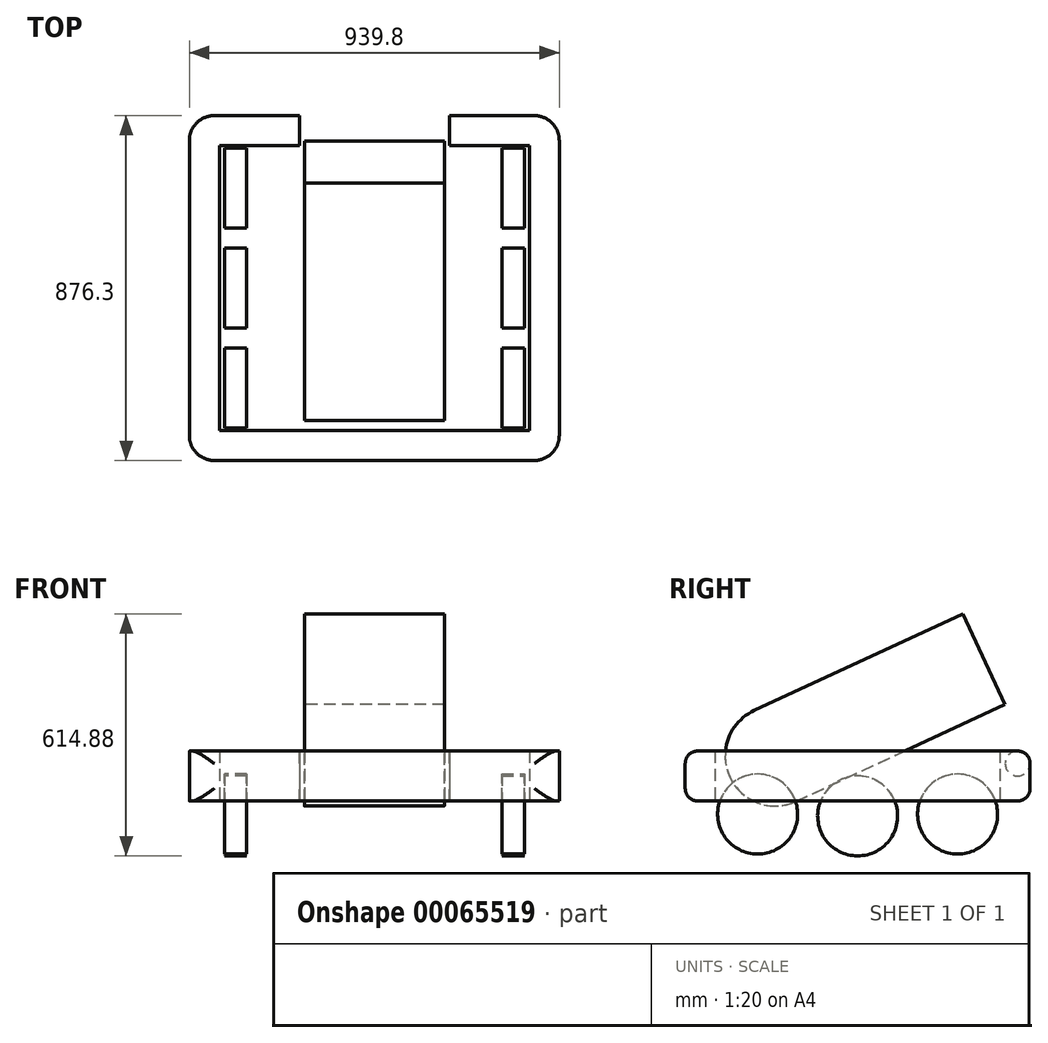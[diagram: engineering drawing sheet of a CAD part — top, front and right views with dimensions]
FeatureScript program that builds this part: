
annotation { "Feature Type Name" : "Feature", "Feature Type Description" : "" }
export const myFeature = defineFeature(function(context is Context, id is Id, definition is map)
    precondition{}
    {
        {
            var Q0;
            Q0=qCreatedBy(makeId("Top.planeOp"),FACE);
            var sketch = newSketch(context, id + "F0", { "sketchPlane" : qUnion([Q0])});
            skLineSegment(sketch, "E0.bottom", {"start": v(-393.7, 361.95) * mm, "end": v(393.7, 361.95) * mm});
            skLineSegment(sketch, "E0.top", {"start": v(-393.7, -361.95) * mm, "end": v(393.7, -361.95) * mm});
            skLineSegment(sketch, "E0.left", {"start": v(-393.7, 361.95) * mm, "end": v(-393.7, -361.95) * mm});
            skLineSegment(sketch, "E0.right", {"start": v(393.7, 361.95) * mm, "end": v(393.7, -361.95) * mm});
            skLineSegment(sketch, "E1", {"start": v(0, 361.95) * mm, "end": v(0, -361.95) * mm, "construction": true});
            skCircle(sketch, "E2", {"center": v(-1228.9, -799.4) * mm, "radius": 127 * mm});
            skCircle(sketch, "E3", {"center": v(0, -155.3) * mm, "radius": 127 * mm});
            skLineSegment(sketch, "E4.bottom", {"start": v(-381, 349.25) * mm, "end": v(-342.9, 349.25) * mm});
            skLineSegment(sketch, "E4.top", {"start": v(-381, 44.45) * mm, "end": v(-342.9, 44.45) * mm});
            skLineSegment(sketch, "E4.left", {"start": v(-381, 349.25) * mm, "end": v(-381, 44.45) * mm});
            skLineSegment(sketch, "E4.right", {"start": v(-342.9, 349.25) * mm, "end": v(-342.9, 44.45) * mm});
            skLineSegment(sketch, "E5.bottom", {"start": v(-381, -44.45) * mm, "end": v(-342.9, -44.45) * mm});
            skLineSegment(sketch, "E5.top", {"start": v(-381, -349.25) * mm, "end": v(-342.9, -349.25) * mm});
            skLineSegment(sketch, "E5.left", {"start": v(-381, -44.45) * mm, "end": v(-381, -349.25) * mm});
            skLineSegment(sketch, "E5.right", {"start": v(-342.9, -44.45) * mm, "end": v(-342.9, -349.25) * mm});
            skLineSegment(sketch, "E6.bottom", {"start": v(342.9, 349.25) * mm, "end": v(381, 349.25) * mm});
            skLineSegment(sketch, "E6.top", {"start": v(342.9, 44.45) * mm, "end": v(381, 44.45) * mm});
            skLineSegment(sketch, "E6.left", {"start": v(342.9, 349.25) * mm, "end": v(342.9, 44.45) * mm});
            skLineSegment(sketch, "E6.right", {"start": v(381, 349.25) * mm, "end": v(381, 44.45) * mm});
            skLineSegment(sketch, "E7.bottom", {"start": v(342.9, -44.45) * mm, "end": v(381, -44.45) * mm});
            skLineSegment(sketch, "E7.top", {"start": v(342.9, -349.25) * mm, "end": v(381, -349.25) * mm});
            skLineSegment(sketch, "E7.left", {"start": v(342.9, -44.45) * mm, "end": v(342.9, -349.25) * mm});
            skLineSegment(sketch, "E7.right", {"start": v(381, -44.45) * mm, "end": v(381, -349.25) * mm});
            skLineSegment(sketch, "E8", {"start": v(393.7, 0) * mm, "end": v(-393.7, 0) * mm, "construction": true});
            skLineSegment(sketch, "E9.bottom", {"start": v(-406.4, 438.15) * mm, "end": v(-190.5, 438.15) * mm});
            skLineSegment(sketch, "E9.top", {"start": v(-406.4, -438.15) * mm, "end": v(406.4, -438.15) * mm});
            skLineSegment(sketch, "E9.left", {"start": v(-469.9, 374.65) * mm, "end": v(-469.9, -374.65) * mm});
            skLineSegment(sketch, "E9.right", {"start": v(469.9, 374.65) * mm, "end": v(469.9, -374.65) * mm});
            skPoint(sketch, "E10.visualSharp", {"position": v(-469.9, 438.15) * mm});
            skArc(sketch, "E10.filletArc", {"start": v(-406.4, 438.15) * mm, "mid": v(-451.3, 419.55) * mm, "end": v(-469.9, 374.65) * mm});
            skPoint(sketch, "E11.visualSharp", {"position": v(-469.9, -438.15) * mm});
            skArc(sketch, "E11.filletArc", {"start": v(-469.9, -374.65) * mm, "mid": v(-451.3, -419.55) * mm, "end": v(-406.4, -438.15) * mm});
            skPoint(sketch, "E12.visualSharp", {"position": v(469.9, -438.15) * mm});
            skArc(sketch, "E12.filletArc", {"start": v(406.4, -438.15) * mm, "mid": v(451.3, -419.55) * mm, "end": v(469.9, -374.65) * mm});
            skPoint(sketch, "E13.visualSharp", {"position": v(469.9, 438.15) * mm});
            skArc(sketch, "E13.filletArc", {"start": v(469.9, 374.65) * mm, "mid": v(451.3, 419.55) * mm, "end": v(406.4, 438.15) * mm});
            skLineSegment(sketch, "E14", {"start": v(-1228.9, -799.4) * mm, "end": v(-505, -799.4) * mm});
            skLineSegment(sketch, "E15", {"start": v(-505, -799.4) * mm, "end": v(282.4, -799.4) * mm});
            skLineSegment(sketch, "E16", {"start": v(190.5, 438.15) * mm, "end": v(190.5, 361.95) * mm});
            skLineSegment(sketch, "E17", {"start": v(-190.5, 438.15) * mm, "end": v(-190.5, 361.95) * mm});
            skLineSegment(sketch, "E18.trimOffspring", {"start": v(190.5, 438.15) * mm, "end": v(406.4, 438.15) * mm});
            skLineSegment(sketch, "E19", {"start": v(-342.9, 196.85) * mm, "end": v(-381, 196.85) * mm, "construction": true});
            skLineSegment(sketch, "E20", {"start": v(-342.9, -196.85) * mm, "end": v(-381, -196.85) * mm, "construction": true});
            skSolve(sketch);
        }
        {
            var Q0;
            Q0=qCreatedBy(makeId("Right.planeOp"),FACE);
            var sketch = newSketch(context, id + "F1", { "sketchPlane" : qUnion([Q0])});
            skCircle(sketch, "E21", {"center": v(196.85, 0) * mm, "radius": 152.4 * mm, "construction": true});
            skCircle(sketch, "E22", {"center": v(-196.85, 0) * mm, "radius": 152.4 * mm, "construction": true});
            skLineSegment(sketch, "E23.0", {"start": v(-44.45, 0) * mm, "end": v(-349.25, 0) * mm, "construction": true});
            skLineSegment(sketch, "E23.1", {"start": v(349.25, 0) * mm, "end": v(44.45, 0) * mm, "construction": true});
            skLineSegment(sketch, "E24.bottom", {"start": v(406.4, 114.3) * mm, "end": v(-406.4, 114.3) * mm});
            skLineSegment(sketch, "E24.top", {"start": v(406.4, -12.7) * mm, "end": v(-406.4, -12.7) * mm});
            skLineSegment(sketch, "E24.left", {"start": v(438.15, 82.55) * mm, "end": v(438.15, 19.05) * mm});
            skLineSegment(sketch, "E24.right", {"start": v(-438.15, 82.55) * mm, "end": v(-438.15, 19.05) * mm});
            skLineSegment(sketch, "E25", {"start": v(-789.47, -152.4) * mm, "end": v(789.47, -152.4) * mm, "construction": true});
            skPoint(sketch, "E26.visualSharp", {"position": v(438.15, 114.3) * mm});
            skArc(sketch, "E26.filletArc", {"start": v(438.15, 82.55) * mm, "mid": v(428.85, 105) * mm, "end": v(406.4, 114.3) * mm});
            skPoint(sketch, "E27.visualSharp", {"position": v(438.15, -12.7) * mm});
            skArc(sketch, "E27.filletArc", {"start": v(406.4, -12.7) * mm, "mid": v(428.85, -3.4) * mm, "end": v(438.15, 19.05) * mm});
            skPoint(sketch, "E28.visualSharp", {"position": v(-438.15, -12.7) * mm});
            skArc(sketch, "E28.filletArc", {"start": v(-438.15, 19.05) * mm, "mid": v(-428.85, -3.4) * mm, "end": v(-406.4, -12.7) * mm});
            skPoint(sketch, "E29.visualSharp", {"position": v(-438.15, 114.3) * mm});
            skArc(sketch, "E29.filletArc", {"start": v(-406.4, 114.3) * mm, "mid": v(-428.85, 105) * mm, "end": v(-438.15, 82.55) * mm});
            skPoint(sketch, "E30", {"position": v(0, -152.4) * mm});
            skLineSegment(sketch, "E31.bottom", {"start": v(1733.48, -38.1) * mm, "end": v(1619.18, -38.1) * mm});
            skLineSegment(sketch, "E31.top", {"start": v(1733.48, -152.4) * mm, "end": v(1619.18, -152.4) * mm});
            skLineSegment(sketch, "E31.left", {"start": v(1733.48, -38.1) * mm, "end": v(1733.48, -152.4) * mm});
            skLineSegment(sketch, "E31.right", {"start": v(1619.18, -38.1) * mm, "end": v(1619.18, -152.4) * mm});
            skLineSegment(sketch, "E32", {"start": v(361.95, 241.3) * mm, "end": v(-361.95, 241.3) * mm});
            skCircle(sketch, "E33", {"center": v(0, 266.7) * mm, "radius": 12.7 * mm});
            skLineSegment(sketch, "E34.bottom", {"start": v(1878.31, -88.9) * mm, "end": v(1840.21, -88.9) * mm});
            skLineSegment(sketch, "E34.top", {"start": v(1878.31, -152.4) * mm, "end": v(1840.21, -152.4) * mm});
            skLineSegment(sketch, "E34.left", {"start": v(1878.31, -88.9) * mm, "end": v(1878.31, -152.4) * mm});
            skLineSegment(sketch, "E34.right", {"start": v(1840.21, -88.9) * mm, "end": v(1840.21, -152.4) * mm});
            skLineSegment(sketch, "E35", {"start": v(535.67, -152.4) * mm, "end": v(535.67, -73.87) * mm});
            skLineSegment(sketch, "E36", {"start": v(535.67, -73.87) * mm, "end": v(1094.47, -152.4) * mm});
            skPoint(sketch, "E36.endSnap0", {"position": v(1859.26, -152.4) * mm});
            skPoint(sketch, "E37", {"position": v(1676.33, -152.4) * mm});
            skLineSegment(sketch, "E38", {"start": v(0, 266.7) * mm, "end": v(-373.39, 342.49) * mm});
            skCircle(sketch, "E39", {"center": v(-373.39, 342.49) * mm, "radius": 12.7 * mm});
            skLineSegment(sketch, "E40.bottom", {"start": v(1374, -152.4) * mm, "end": v(1450.2, -152.4) * mm});
            skLineSegment(sketch, "E40.top", {"start": v(1374, -76.2) * mm, "end": v(1450.2, -76.2) * mm});
            skLineSegment(sketch, "E40.left", {"start": v(1374, -152.4) * mm, "end": v(1374, -76.2) * mm});
            skLineSegment(sketch, "E40.right", {"start": v(1450.2, -152.4) * mm, "end": v(1450.2, -76.2) * mm});
            skLineSegment(sketch, "E41", {"start": v(-61.4, -69.85) * mm, "end": v(61.4, -69.85) * mm});
            skCircle(sketch, "E42", {"center": v(-663.32, -25.4) * mm, "radius": 127 * mm});
            skCircle(sketch, "E43", {"center": v(3436.9, 34.7) * mm, "radius": 39.75 * mm});
            skCircle(sketch, "E44", {"center": v(3218.47, -112.65) * mm, "radius": 39.75 * mm});
            skCircle(sketch, "E45", {"center": v(2761.27, -112.65) * mm, "radius": 39.75 * mm});
            skLineSegment(sketch, "E46", {"start": v(2761.27, -112.65) * mm, "end": v(3218.47, -112.65) * mm, "construction": true});
            skLineSegment(sketch, "E47", {"start": v(3436.9, 34.7) * mm, "end": v(3218.47, -112.65) * mm, "construction": true});
            skLineSegment(sketch, "E48", {"start": v(3459.14, 1.74) * mm, "end": v(3240.7, -145.6) * mm});
            skLineSegment(sketch, "E49", {"start": v(3428.44, 73.53) * mm, "end": v(2752.8, -73.81) * mm});
            skLineSegment(sketch, "E50.bottom", {"start": v(2348.21, -88.9) * mm, "end": v(2310.11, -88.9) * mm});
            skLineSegment(sketch, "E50.top", {"start": v(2348.21, -152.4) * mm, "end": v(2310.11, -152.4) * mm});
            skLineSegment(sketch, "E50.left", {"start": v(2348.21, -88.9) * mm, "end": v(2348.21, -152.4) * mm});
            skLineSegment(sketch, "E50.right", {"start": v(2310.11, -88.9) * mm, "end": v(2310.11, -152.4) * mm});
            skCircle(sketch, "E51", {"center": v(2989.87, -112.65) * mm, "radius": 39.75 * mm});
            skLineSegment(sketch, "E52", {"start": v(2761.27, -152.4) * mm, "end": v(3218.47, -152.4) * mm});
            skSolve(sketch);
        }
        {
            var Q0;
            Q0=qCreatedBy(makeId("Top.planeOp"),FACE);
            var sketch = newSketch(context, id + "F2", { "sketchPlane" : qUnion([Q0])});
            skLineSegment(sketch, "E53.bottom", {"start": v(-4052.58, 2835.77) * mm, "end": v(4050.02, 2835.77) * mm});
            skLineSegment(sketch, "E53.top", {"start": v(-4050.02, -13648.83) * mm, "end": v(4050.02, -13648.83) * mm});
            skLineSegment(sketch, "E53.right", {"start": v(4050.02, 2835.77) * mm, "end": v(4050.02, -13648.83) * mm});
            skLineSegment(sketch, "E54", {"start": v(-4052.58, 2835.77) * mm, "end": v(-4052.58, -2659.1) * mm});
            skLineSegment(sketch, "E55", {"start": v(-4052.58, -2659.1) * mm, "end": v(-4052.58, -8153.97) * mm});
            skLineSegment(sketch, "E56", {"start": v(-4052.58, -8153.97) * mm, "end": v(-4050.02, -13648.83) * mm});
            skLineSegment(sketch, "E57", {"start": v(-2376.18, -8153.97) * mm, "end": v(4050.02, -8153.97) * mm, "construction": true});
            skLineSegment(sketch, "E58", {"start": v(-4052.58, -2659.1) * mm, "end": v(2373.62, -2659.1) * mm, "construction": true});
            skLineSegment(sketch, "E59.bottom", {"start": v(2373.62, -2058.4) * mm, "end": v(-4052.58, -2058.4) * mm});
            skLineSegment(sketch, "E59.top", {"start": v(2373.62, -3259.81) * mm, "end": v(-4052.58, -3259.81) * mm});
            skLineSegment(sketch, "E59.right", {"start": v(-4052.58, -2058.4) * mm, "end": v(-4052.58, -3259.81) * mm});
            skLineSegment(sketch, "E60.bottom", {"start": v(4050.02, -8754.68) * mm, "end": v(-2376.18, -8754.68) * mm});
            skLineSegment(sketch, "E60.top", {"start": v(4050.02, -7553.26) * mm, "end": v(-2376.18, -7553.26) * mm});
            skLineSegment(sketch, "E60.left", {"start": v(4050.02, -8754.68) * mm, "end": v(4050.02, -7553.26) * mm});
            skLineSegment(sketch, "E61", {"start": v(0, 2835.77) * mm, "end": v(0, -13648.83) * mm, "construction": true});
            skLineSegment(sketch, "E62", {"start": v(-609.6, 2835.77) * mm, "end": v(-304.8, 2307.84) * mm, "construction": true});
            skLineSegment(sketch, "E63", {"start": v(-304.8, 2307.84) * mm, "end": v(304.8, 2307.84) * mm, "construction": true});
            skLineSegment(sketch, "E64", {"start": v(304.8, 2307.84) * mm, "end": v(609.6, 2835.77) * mm, "construction": true});
            skLineSegment(sketch, "E65", {"start": v(2373.62, 2835.77) * mm, "end": v(2373.62, -4466.73) * mm});
            skLineSegment(sketch, "E66", {"start": v(2373.62, -4466.73) * mm, "end": v(4050.02, -4466.73) * mm});
            skLineSegment(sketch, "E67", {"start": v(-4052.58, -6346.33) * mm, "end": v(-2376.18, -6346.33) * mm});
            skLineSegment(sketch, "E68", {"start": v(-2376.18, -6346.33) * mm, "end": v(-2376.18, -13648.83) * mm});
            skLineSegment(sketch, "E69", {"start": v(-762, 2835.77) * mm, "end": v(-381, 2175.85) * mm});
            skLineSegment(sketch, "E70", {"start": v(-381, 2175.85) * mm, "end": v(381, 2175.85) * mm});
            skLineSegment(sketch, "E71", {"start": v(381, 2175.85) * mm, "end": v(762, 2835.77) * mm});
            skLineSegment(sketch, "E72", {"start": v(-1533.48, 2835.77) * mm, "end": v(-1533.48, 2302.37) * mm});
            skLineSegment(sketch, "E73", {"start": v(-1533.48, 2302.37) * mm, "end": v(-1228.68, 1774.44) * mm});
            skLineSegment(sketch, "E74", {"start": v(-1228.68, 1774.44) * mm, "end": v(-304.8, 1241.04) * mm});
            skLineSegment(sketch, "E75", {"start": v(-304.8, 1241.04) * mm, "end": v(304.8, 1241.04) * mm});
            skLineSegment(sketch, "E76", {"start": v(304.8, 1241.04) * mm, "end": v(1228.68, 1774.44) * mm});
            skLineSegment(sketch, "E77", {"start": v(1228.68, 1774.44) * mm, "end": v(1533.48, 2302.37) * mm});
            skLineSegment(sketch, "E78", {"start": v(1533.48, 2302.37) * mm, "end": v(1533.48, 2835.77) * mm});
            skLineSegment(sketch, "E79", {"start": v(457.2, 2571.8) * mm, "end": v(1381.08, 2038.4) * mm, "construction": true});
            skLineSegment(sketch, "E80", {"start": v(0, 2307.84) * mm, "end": v(0, 1241.04) * mm, "construction": true});
            skArc(sketch, "E81", {"start": v(-2032, 2835.77) * mm, "mid": v(0, 803.77) * mm, "end": v(2032, 2835.77) * mm, "construction": true});
            skArc(sketch, "E82", {"start": v(-4052.58, -1011.62) * mm, "mid": v(-1.85, -2752.23) * mm, "end": v(4050.02, -1014.3) * mm, "construction": true});
            skArc(sketch, "E83", {"start": v(-762, 2835.77) * mm, "mid": v(0, 2073.77) * mm, "end": v(762, 2835.77) * mm, "construction": true});
            skSolve(sketch);
        }
        {
            var Q0;
            Q0=qCreatedBy(makeId("Right.planeOp"),FACE);
            var sketch = newSketch(context, id + "F3", { "sketchPlane" : qUnion([Q0])});
            skLineSegment(sketch, "E84.bottom", {"start": v(406.4, 114.3) * mm, "end": v(-406.4, 114.3) * mm, "construction": true});
            skLineSegment(sketch, "E84.top", {"start": v(406.4, -12.7) * mm, "end": v(-406.4, -12.7) * mm, "construction": true});
            skLineSegment(sketch, "E84.left", {"start": v(438.15, 82.55) * mm, "end": v(438.15, 19.05) * mm, "construction": true});
            skLineSegment(sketch, "E84.right", {"start": v(-438.15, 82.55) * mm, "end": v(-438.15, 19.05) * mm, "construction": true});
            skPoint(sketch, "E85.visualSharp", {"position": v(438.15, 114.3) * mm});
            skArc(sketch, "E85.filletArc", {"start": v(438.15, 82.55) * mm, "mid": v(428.85, 105) * mm, "end": v(406.4, 114.3) * mm, "construction": true});
            skPoint(sketch, "E86.visualSharp", {"position": v(438.15, -12.7) * mm});
            skArc(sketch, "E86.filletArc", {"start": v(406.4, -12.7) * mm, "mid": v(428.85, -3.4) * mm, "end": v(438.15, 19.05) * mm, "construction": true});
            skPoint(sketch, "E87.visualSharp", {"position": v(-438.15, -12.7) * mm});
            skArc(sketch, "E87.filletArc", {"start": v(-438.15, 19.05) * mm, "mid": v(-428.85, -3.4) * mm, "end": v(-406.4, -12.7) * mm, "construction": true});
            skPoint(sketch, "E88.visualSharp", {"position": v(-438.15, 114.3) * mm});
            skArc(sketch, "E88.filletArc", {"start": v(-406.4, 114.3) * mm, "mid": v(-428.85, 105) * mm, "end": v(-438.15, 82.55) * mm, "construction": true});
            skLineSegment(sketch, "E89", {"start": v(-361.95, 114.3) * mm, "end": v(-361.95, -12.7) * mm, "construction": true});
            skLineSegment(sketch, "E90", {"start": v(361.95, 114.3) * mm, "end": v(361.95, -12.7) * mm, "construction": true});
            skArc(sketch, "E91", {"start": v(-262.95, 216.83) * mm, "mid": v(-324.78, 48.2) * mm, "end": v(-156.15, -13.63) * mm});
            skLineSegment(sketch, "E92", {"start": v(-156.15, -13.63) * mm, "end": v(373.9, 232.03) * mm});
            skLineSegment(sketch, "E93", {"start": v(373.9, 232.03) * mm, "end": v(267.09, 462.48) * mm});
            skLineSegment(sketch, "E94", {"start": v(267.09, 462.48) * mm, "end": v(-262.95, 216.83) * mm});
            skCircle(sketch, "E95", {"center": v(675.83, -25.4) * mm, "radius": 127 * mm});
            skLineSegment(sketch, "E96", {"start": v(-209.55, 101.6) * mm, "end": v(320.5, 347.26) * mm, "construction": true});
            skLineSegment(sketch, "E97.0", {"start": v(-789.47, -152.4) * mm, "end": v(789.47, -152.4) * mm, "construction": true});
            skLineSegment(sketch, "E98", {"start": v(789.47, 241.3) * mm, "end": v(-789.47, 241.3) * mm, "construction": true});
            skPoint(sketch, "E99", {"position": v(119.88, 114.3) * mm});
            skLineSegment(sketch, "E100", {"start": v(-209.55, 101.6) * mm, "end": v(-209.55, -12.7) * mm, "construction": true});
            skSolve(sketch);
        }
        {
            var Q0;
            Q0=qCreatedBy(makeId("Right.planeOp"),FACE);
            var sketch = newSketch(context, id + "F4", { "sketchPlane" : qUnion([Q0])});
            skArc(sketch, "E101.0", {"start": v(438.15, 82.55) * mm, "mid": v(428.85, 105) * mm, "end": v(406.4, 114.3) * mm, "construction": true});
            skLineSegment(sketch, "E101.1", {"start": v(438.15, 82.55) * mm, "end": v(438.15, 19.05) * mm, "construction": true});
            skArc(sketch, "E101.2", {"start": v(406.4, -12.7) * mm, "mid": v(428.85, -3.4) * mm, "end": v(438.15, 19.05) * mm, "construction": true});
            skLineSegment(sketch, "E101.3", {"start": v(406.4, -12.7) * mm, "end": v(-406.4, -12.7) * mm, "construction": true});
            skLineSegment(sketch, "E101.4", {"start": v(406.4, 114.3) * mm, "end": v(-406.4, 114.3) * mm, "construction": true});
            skArc(sketch, "E101.5", {"start": v(-406.4, 114.3) * mm, "mid": v(-428.85, 105) * mm, "end": v(-438.15, 82.55) * mm, "construction": true});
            skLineSegment(sketch, "E101.6", {"start": v(-438.15, 82.55) * mm, "end": v(-438.15, 19.05) * mm, "construction": true});
            skArc(sketch, "E101.7", {"start": v(-438.15, 19.05) * mm, "mid": v(-428.85, -3.4) * mm, "end": v(-406.4, -12.7) * mm, "construction": true});
            skLineSegment(sketch, "E102.0", {"start": v(-361.95, 114.3) * mm, "end": v(-361.95, -12.7) * mm, "construction": true});
            skLineSegment(sketch, "E102.1", {"start": v(361.95, 114.3) * mm, "end": v(361.95, -12.7) * mm, "construction": true});
            skLineSegment(sketch, "E103.0", {"start": v(-789.47, -152.4) * mm, "end": v(789.47, -152.4) * mm, "construction": true});
            skLineSegment(sketch, "E103.1", {"start": v(789.47, 241.3) * mm, "end": v(-789.47, 241.3) * mm, "construction": true});
            skCircle(sketch, "E104", {"center": v(254, -46.04) * mm, "radius": 101.6 * mm});
            skCircle(sketch, "E105", {"center": v(0, -50.8) * mm, "radius": 101.6 * mm});
            skCircle(sketch, "E106", {"center": v(-254, -46.04) * mm, "radius": 101.6 * mm});
            skLineSegment(sketch, "E107", {"start": v(0, -12.7) * mm, "end": v(0, 114.3) * mm, "construction": true});
            skCircle(sketch, "E108", {"center": v(0, -50.8) * mm, "radius": 83.82 * mm, "construction": true});
            skCircle(sketch, "E109", {"center": v(254, -46.04) * mm, "radius": 83.82 * mm, "construction": true});
            skCircle(sketch, "E110", {"center": v(-254, -46.04) * mm, "radius": 83.82 * mm, "construction": true});
            skCircle(sketch, "E111", {"center": v(-126.52, -23) * mm, "radius": 45.72 * mm});
            skCircle(sketch, "E112", {"center": v(126.52, -23) * mm, "radius": 45.72 * mm});
            skLineSegment(sketch, "E113", {"start": v(-161.88, -88.9) * mm, "end": v(-94.19, -88.9) * mm, "construction": true});
            skCircle(sketch, "E114", {"center": v(-92.77, 18.3) * mm, "radius": 32.39 * mm, "construction": true});
            skCircle(sketch, "E115", {"center": v(-92.77, 18.3) * mm, "radius": 7.62 * mm});
            skCircle(sketch, "E116", {"center": v(-160.28, 18.3) * mm, "radius": 32.39 * mm, "construction": true});
            skLineSegment(sketch, "E117", {"start": v(-126.52, -23) * mm, "end": v(-126.52, -12.7) * mm, "construction": true});
            skSolve(sketch);
        }
        {
            var Q0;
            Q0=makeQuery(id+"F0.imprint","IMPRINT",FACE,{"disambiguationData":[TD([[makeQuery(id+"F0.imprint","IMPRINT",EDGE,{"derivedFrom":sQuery(id+"F0.wireOp",EDGE,"E0.top")}),-1.0]])]});
            extrude(context, id + "F5", {"entities" : qUnion([Q0]), "depth" : 203.2 * mm, "hasSecondDirection" : true, "secondDirectionOppositeDirection" : true, "secondDirectionDepth" : 101.6 * mm});
        }
        {
            var Q0;
            Q0=makeQuery(id+"F1.imprint","IMPRINT",FACE,{"disambiguationData":[TD([[makeQuery(id+"F1.imprint","IMPRINT",EDGE,{"derivedFrom":sQuery(id+"F1.wireOp",EDGE,"E24.bottom")}),1.0]])]});
            var Q1;
            Q1=makeQuery(id+"F5.opExtrude","SWEPT_FACE",FACE,{"disambiguationData":[OSD([sQuery(id+"F0.wireOp",EDGE,"E9.left")])]});
            var Q2;
            Q2=makeQuery(id+"F5.opExtrude","SWEPT_FACE",FACE,{"disambiguationData":[OSD([sQuery(id+"F0.wireOp",EDGE,"E9.right")])]});
            extrude(context, id + "F6", {"entities" : qUnion([Q0]), "operationType" : NewBodyOperationType.INTERSECT, "endBound" : BoundingType.UP_TO_SURFACE, "oppositeDirection" : true, "endBoundEntityFace" : qUnion([Q1]), "depth" : 25.4 * mm, "hasSecondDirection" : true, "secondDirectionBound" : SecondDirectionBoundingType.UP_TO_SURFACE, "secondDirectionOppositeDirection" : false, "secondDirectionBoundEntityFace" : qUnion([Q2]), "secondDirectionDepth" : 25.4 * mm});
        }
        {
            var Q0;
            {var subQ0=sQuery(id+"F4.wireOp",EDGE,"E112");var subQ1=sQuery(id+"F4.wireOp",EDGE,"E104");var subQ2=makeQuery(id+"F4.imprint","INTERSECT",VERTEX,{"disambiguationData":[OD(0.0)],"derivedFrom":[subQ1,subQ0]});Q0=makeQuery(id+"F4.imprint","IMPRINT",FACE,{"disambiguationData":[TD([[makeQuery(id+"F4.imprint","IMPRINT",EDGE,{"disambiguationData":[TD([[subQ2,1.0]])],"derivedFrom":subQ1}),1.0]])]});}
            var Q1;
            {var subQ0=sQuery(id+"F4.wireOp",EDGE,"E112");var subQ1=sQuery(id+"F4.wireOp",EDGE,"E104");var subQ2=makeQuery(id+"F4.imprint","INTERSECT",VERTEX,{"disambiguationData":[OD(0.0)],"derivedFrom":[subQ1,subQ0]});Q1=makeQuery(id+"F4.imprint","IMPRINT",FACE,{"disambiguationData":[TD([[makeQuery(id+"F4.imprint","IMPRINT",EDGE,{"disambiguationData":[TD([[subQ2,-1.0]])],"derivedFrom":subQ1}),1.0]])]});}
            var Q2;
            {var subQ0=sQuery(id+"F4.wireOp",EDGE,"E111");var subQ1=sQuery(id+"F4.wireOp",EDGE,"E105");var subQ2=makeQuery(id+"F4.imprint","INTERSECT",VERTEX,{"disambiguationData":[OD(0.0)],"derivedFrom":[subQ1,subQ0]});Q2=makeQuery(id+"F4.imprint","IMPRINT",FACE,{"disambiguationData":[TD([[makeQuery(id+"F4.imprint","IMPRINT",EDGE,{"disambiguationData":[TD([[subQ2,1.0]])],"derivedFrom":subQ1}),1.0]])]});}
            var Q3;
            {var subQ0=sQuery(id+"F4.wireOp",EDGE,"E112");var subQ1=sQuery(id+"F4.wireOp",EDGE,"E105");var subQ2=makeQuery(id+"F4.imprint","INTERSECT",VERTEX,{"disambiguationData":[OD(0.0)],"derivedFrom":[subQ1,subQ0]});Q3=makeQuery(id+"F4.imprint","IMPRINT",FACE,{"disambiguationData":[TD([[makeQuery(id+"F4.imprint","IMPRINT",EDGE,{"disambiguationData":[TD([[subQ2,1.0]])],"derivedFrom":subQ1}),1.0]])]});}
            var Q4;
            {var subQ0=sQuery(id+"F4.wireOp",EDGE,"E111");var subQ1=sQuery(id+"F4.wireOp",EDGE,"E105");var subQ2=makeQuery(id+"F4.imprint","INTERSECT",VERTEX,{"disambiguationData":[OD(0.0)],"derivedFrom":[subQ1,subQ0]});Q4=makeQuery(id+"F4.imprint","IMPRINT",FACE,{"disambiguationData":[TD([[makeQuery(id+"F4.imprint","IMPRINT",EDGE,{"disambiguationData":[TD([[subQ2,-1.0]])],"derivedFrom":subQ1}),1.0]])]});}
            var Q5;
            {var subQ0=sQuery(id+"F4.wireOp",EDGE,"E111");var subQ1=sQuery(id+"F4.wireOp",EDGE,"E106");var subQ2=makeQuery(id+"F4.imprint","INTERSECT",VERTEX,{"disambiguationData":[OD(0.0)],"derivedFrom":[subQ1,subQ0]});Q5=makeQuery(id+"F4.imprint","IMPRINT",FACE,{"disambiguationData":[TD([[makeQuery(id+"F4.imprint","IMPRINT",EDGE,{"disambiguationData":[TD([[subQ2,1.0]])],"derivedFrom":subQ1}),1.0]])]});}
            var Q6;
            {var subQ0=sQuery(id+"F4.wireOp",EDGE,"E111");var subQ1=sQuery(id+"F4.wireOp",EDGE,"E106");var subQ2=makeQuery(id+"F4.imprint","INTERSECT",VERTEX,{"disambiguationData":[OD(0.0)],"derivedFrom":[subQ1,subQ0]});Q6=makeQuery(id+"F4.imprint","IMPRINT",FACE,{"disambiguationData":[TD([[makeQuery(id+"F4.imprint","IMPRINT",EDGE,{"disambiguationData":[TD([[subQ2,-1.0]])],"derivedFrom":subQ1}),1.0]])]});}
            extrude(context, id + "F7", {"entities" : qUnion([Q0, Q1, Q2, Q3, Q4, Q5, Q6]), "depth" : 57.15 * mm});
        }
        {
            var Q0;
            Q0=makeQuery(id+"F7.opExtrude","SWEPT_BODY",BODY,{"disambiguationData":[OSD([sQuery(id+"F4.wireOp",EDGE,"E104")])]});
            var Q1;
            Q1=makeQuery(id+"F7.opExtrude","SWEPT_BODY",BODY,{"disambiguationData":[OSD([sQuery(id+"F4.wireOp",EDGE,"E105")])]});
            var Q2;
            Q2=makeQuery(id+"F7.opExtrude","SWEPT_BODY",BODY,{"disambiguationData":[OSD([sQuery(id+"F4.wireOp",EDGE,"E106")])]});
            var Q3;
            Q3=sQuery(id+"F0.wireOp",EDGE,"E8");
            transform(context, id + "F8", {"entities" : qUnion([Q0, Q1, Q2]), "transformType" : TransformType.TRANSLATION_DISTANCE, "transformDirection" : qUnion([Q3]), "distance" : 381 * mm, "makeCopy" : false});
        }
        {
            var Q0;
            Q0=makeQuery(id+"F7.opExtrude","SWEPT_BODY",BODY,{"disambiguationData":[OSD([sQuery(id+"F4.wireOp",EDGE,"E104")])]});
            var Q1;
            Q1=makeQuery(id+"F7.opExtrude","SWEPT_BODY",BODY,{"disambiguationData":[OSD([sQuery(id+"F4.wireOp",EDGE,"E105")])]});
            var Q2;
            Q2=makeQuery(id+"F7.opExtrude","SWEPT_BODY",BODY,{"disambiguationData":[OSD([sQuery(id+"F4.wireOp",EDGE,"E106")])]});
            var Q3;
            Q3=qCreatedBy(makeId("Right.planeOp"),FACE);
            mirror(context, id + "F9", {"entities" : qUnion([Q0, Q1, Q2]), "mirrorPlane" : qUnion([Q3])});
        }
        {
            var Q0;
            Q0=makeQuery(id+"F3.imprint","IMPRINT",FACE,{"disambiguationData":[TD([[makeQuery(id+"F3.imprint","IMPRINT",EDGE,{"derivedFrom":sQuery(id+"F3.wireOp",EDGE,"E91")}),1.0]])]});
            extrude(context, id + "F10", {"entities" : qUnion([Q0]), "endBound" : BoundingType.SYMMETRIC, "depth" : 355.6 * mm});
        }
    });
